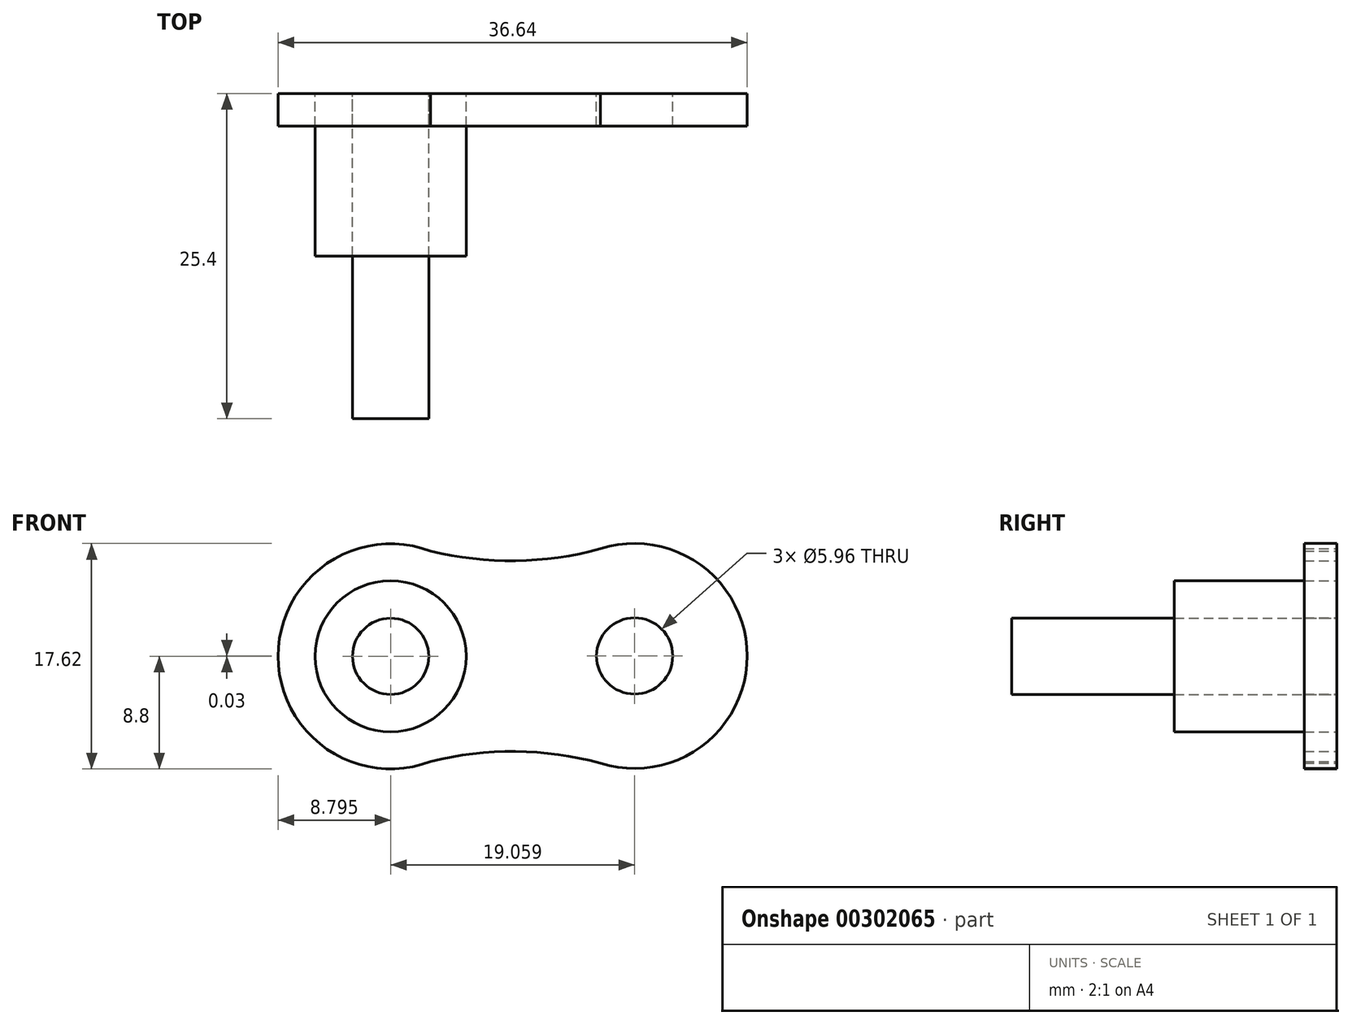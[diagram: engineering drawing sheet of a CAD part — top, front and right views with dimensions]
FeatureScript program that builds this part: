
annotation { "Feature Type Name" : "Feature", "Feature Type Description" : "" }
export const myFeature = defineFeature(function(context is Context, id is Id, definition is map)
    precondition{}
    {
        {
            var Q0;
            Q0=qCreatedBy(makeId("Front.planeOp"),FACE);
            var sketch = newSketch(context, id + "F0", { "sketchPlane" : qUnion([Q0])});
            skCircle(sketch, "E0", {"center": v(-9.53, 0) * mm, "radius": 2.98 * mm});
            skArc(sketch, "E1", {"start": v(-6.4, 8.22) * mm, "mid": v(-18.32, 0) * mm, "end": v(-6.4, -8.22) * mm});
            skArc(sketch, "E2", {"start": v(6.86, -8.34) * mm, "mid": v(18.32, 0.03) * mm, "end": v(6.86, 8.4) * mm});
            skArc(sketch, "E3.0", {"start": v(6.86, 8.4) * mm, "mid": v(0.24, 7.47) * mm, "end": v(-6.4, 8.22) * mm});
            skArc(sketch, "E4.0", {"start": v(-6.4, -8.22) * mm, "mid": v(0.24, -7.44) * mm, "end": v(6.86, -8.34) * mm});
            skCircle(sketch, "E5", {"center": v(9.53, 0.03) * mm, "radius": 2.98 * mm});
            skSolve(sketch);
        }
        {
            var Q0;
            Q0 = qSketchRegion(id + "F0", true);
            extrude(context, id + "F1", {"entities" : qUnion([Q0]), "depth" : 2.54 * mm});
        }
        {
            var Q0;
            Q0=makeQuery(id+"F0.imprint","IMPRINT",FACE,{"disambiguationData":[TD([[makeQuery(id+"F0.imprint","IMPRINT",EDGE,{"derivedFrom":sQuery(id+"F0.wireOp",EDGE,"E0")}),1.0]])]});
            extrude(context, id + "F2", {"entities" : qUnion([Q0]), "depth" : 25.4 * mm});
        }
        {
            var Q0;
            Q0=makeQuery(id+"F0.imprint","IMPRINT",FACE,{"disambiguationData":[TD([[makeQuery(id+"F0.imprint","IMPRINT",EDGE,{"derivedFrom":sQuery(id+"F0.wireOp",EDGE,"E0")}),-1.0]])]});
            var sketch = newSketch(context, id + "F3", { "sketchPlane" : qUnion([Q0])});
            skCircle(sketch, "E6.0", {"center": v(-9.53, 0) * mm, "radius": 5.9 * mm});
            skSolve(sketch);
        }
        {
            var Q0;
            Q0=makeQuery(id+"F3.imprint","IMPRINT",FACE,{"disambiguationData":[TD([[makeQuery(id+"F3.imprint","IMPRINT",EDGE,{"derivedFrom":sQuery(id+"F3.wireOp",EDGE,"E6.0")}),1.0]])]});
            extrude(context, id + "F4", {"entities" : qUnion([Q0]), "depth" : 12.7 * mm});
        }
    });
